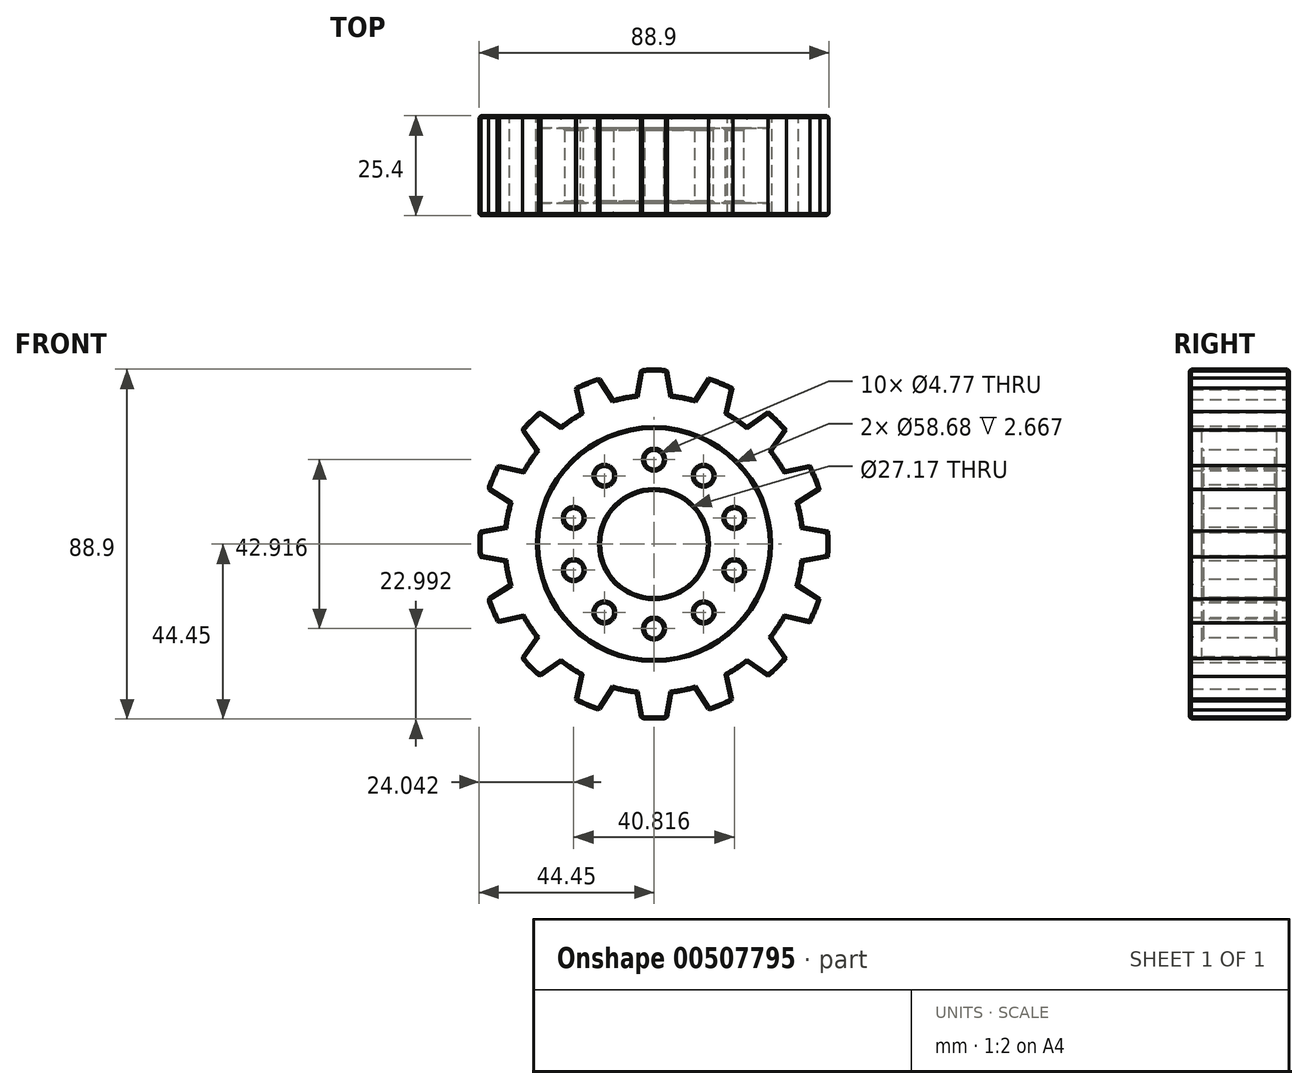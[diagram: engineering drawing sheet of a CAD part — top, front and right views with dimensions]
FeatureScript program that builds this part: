
annotation { "Feature Type Name" : "Feature", "Feature Type Description" : "" }
export const myFeature = defineFeature(function(context is Context, id is Id, definition is map)
    precondition{}
    {
        {
            var Q0;
            Q0=qCreatedBy(makeId("Front.planeOp"),FACE);
            var sketch = newSketch(context, id + "F0", { "sketchPlane" : qUnion([Q0])});
            skCircle(sketch, "E0", {"center": v(0, 0) * mm, "radius": 38.1 * mm});
            skCircle(sketch, "E1.0", {"center": v(0, 0) * mm, "radius": 44.45 * mm});
            skLineSegment(sketch, "E2", {"start": v(3.3, 44.33) * mm, "end": v(4.45, 37.84) * mm});
            skLineSegment(sketch, "E3.MirrorCS", {"start": v(-3.3, 44.33) * mm, "end": v(-4.45, 37.84) * mm});
            skLineSegment(sketch, "E4.1.0", {"start": v(-20.02, 39.69) * mm, "end": v(-18.6, 33.26) * mm});
            skLineSegment(sketch, "E4.1.1", {"start": v(-13.9, 42.22) * mm, "end": v(-10.37, 36.66) * mm});
            skLineSegment(sketch, "E4.2.0", {"start": v(-33.68, 29) * mm, "end": v(-29.9, 23.6) * mm});
            skLineSegment(sketch, "E4.2.1", {"start": v(-29, 33.68) * mm, "end": v(-23.6, 29.9) * mm});
            skLineSegment(sketch, "E4.3.0", {"start": v(-42.22, 13.9) * mm, "end": v(-36.66, 10.37) * mm});
            skLineSegment(sketch, "E4.3.1", {"start": v(-39.69, 20.02) * mm, "end": v(-33.26, 18.6) * mm});
            skLineSegment(sketch, "E4.4.0", {"start": v(-44.33, -3.3) * mm, "end": v(-37.84, -4.45) * mm});
            skLineSegment(sketch, "E4.4.1", {"start": v(-44.33, 3.3) * mm, "end": v(-37.84, 4.45) * mm});
            skLineSegment(sketch, "E4.5.0", {"start": v(-39.69, -20.02) * mm, "end": v(-33.26, -18.6) * mm});
            skLineSegment(sketch, "E4.5.1", {"start": v(-42.22, -13.9) * mm, "end": v(-36.66, -10.37) * mm});
            skLineSegment(sketch, "E4.6.0", {"start": v(-29, -33.68) * mm, "end": v(-23.6, -29.9) * mm});
            skLineSegment(sketch, "E4.6.1", {"start": v(-33.68, -29) * mm, "end": v(-29.9, -23.6) * mm});
            skLineSegment(sketch, "E4.7.0", {"start": v(-13.9, -42.22) * mm, "end": v(-10.37, -36.66) * mm});
            skLineSegment(sketch, "E4.7.1", {"start": v(-20.02, -39.69) * mm, "end": v(-18.6, -33.26) * mm});
            skLineSegment(sketch, "E4.8.0", {"start": v(3.3, -44.33) * mm, "end": v(4.45, -37.84) * mm});
            skLineSegment(sketch, "E4.8.1", {"start": v(-3.3, -44.33) * mm, "end": v(-4.45, -37.84) * mm});
            skLineSegment(sketch, "E4.9.0", {"start": v(20.02, -39.69) * mm, "end": v(18.6, -33.26) * mm});
            skLineSegment(sketch, "E4.9.1", {"start": v(13.9, -42.22) * mm, "end": v(10.37, -36.66) * mm});
            skCircle(sketch, "E5", {"center": v(0, 0) * mm, "radius": 29.34 * mm});
            skCircle(sketch, "E6", {"center": v(0, 0) * mm, "radius": 13.59 * mm});
            skCircle(sketch, "E7", {"center": v(0, 21.46) * mm, "radius": 2.39 * mm});
            skCircle(sketch, "E8.1.0", {"center": v(-12.61, 17.36) * mm, "radius": 2.39 * mm});
            skCircle(sketch, "E8.2.0", {"center": v(-20.4, 6.63) * mm, "radius": 2.39 * mm});
            skCircle(sketch, "E8.3.0", {"center": v(-20.4, -6.63) * mm, "radius": 2.39 * mm});
            skCircle(sketch, "E8.4.0", {"center": v(-12.61, -17.36) * mm, "radius": 2.39 * mm});
            skCircle(sketch, "E9.1.5.0", {"center": v(0, -21.46) * mm, "radius": 2.39 * mm});
            skCircle(sketch, "E10.1.6.0", {"center": v(12.61, -17.36) * mm, "radius": 2.39 * mm});
            skCircle(sketch, "E10.1.7.0", {"center": v(20.4, -6.63) * mm, "radius": 2.39 * mm});
            skCircle(sketch, "E11.1.8.0", {"center": v(20.4, 6.63) * mm, "radius": 2.39 * mm});
            skCircle(sketch, "E11.1.9.0", {"center": v(12.61, 17.36) * mm, "radius": 2.39 * mm});
            skLineSegment(sketch, "E12.2.10.0", {"start": v(33.68, -29) * mm, "end": v(29.9, -23.6) * mm});
            skLineSegment(sketch, "E12.3.10.0", {"start": v(29, -33.68) * mm, "end": v(23.6, -29.9) * mm});
            skLineSegment(sketch, "E12.2.11.0", {"start": v(42.22, -13.9) * mm, "end": v(36.66, -10.37) * mm});
            skLineSegment(sketch, "E12.3.11.0", {"start": v(39.69, -20.02) * mm, "end": v(33.26, -18.6) * mm});
            skLineSegment(sketch, "E13.2.12.0", {"start": v(44.33, 3.3) * mm, "end": v(37.84, 4.45) * mm});
            skLineSegment(sketch, "E13.3.12.0", {"start": v(44.33, -3.3) * mm, "end": v(37.84, -4.45) * mm});
            skLineSegment(sketch, "E14.2.13.0", {"start": v(39.69, 20.02) * mm, "end": v(33.26, 18.6) * mm});
            skLineSegment(sketch, "E14.3.13.0", {"start": v(42.22, 13.9) * mm, "end": v(36.66, 10.37) * mm});
            skLineSegment(sketch, "E15.2.14.0", {"start": v(29, 33.68) * mm, "end": v(23.6, 29.9) * mm});
            skLineSegment(sketch, "E15.3.14.0", {"start": v(33.68, 29) * mm, "end": v(29.9, 23.6) * mm});
            skLineSegment(sketch, "E16.2.15.0", {"start": v(13.9, 42.22) * mm, "end": v(10.37, 36.66) * mm});
            skLineSegment(sketch, "E16.3.15.0", {"start": v(20.02, 39.69) * mm, "end": v(18.6, 33.26) * mm});
            skSolve(sketch);
        }
        {
            var Q0;
            Q0 = qSketchRegion(id + "F0", true);
            var Q1;
            Q1=makeQuery(id+"F0.imprint","IMPRINT",FACE,{"disambiguationData":[TD([[makeQuery(id+"F0.imprint","IMPRINT",EDGE,{"derivedFrom":sQuery(id+"F0.wireOp",EDGE,"E0")}),-1.0]])]});
            extrude(context, id + "F1", {"entities" : qUnion([Q0, Q1]), "endBound" : BoundingType.SYMMETRIC, "depth" : 25.4 * mm});
        }
        {
            var Q0;
            Q0=makeQuery(id+"F0.imprint","IMPRINT",FACE,{"disambiguationData":[TD([[makeQuery(id+"F0.imprint","IMPRINT",EDGE,{"derivedFrom":sQuery(id+"F0.wireOp",EDGE,"E0")}),1.0]])]});
            extrude(context, id + "F2", {"entities" : qUnion([Q0]), "operationType" : NewBodyOperationType.ADD, "endBound" : BoundingType.SYMMETRIC, "depth" : 25.4 * mm});
        }
        {
            var Q0;
            Q0=makeQuery(id+"F0.imprint","IMPRINT",FACE,{"disambiguationData":[TD([[makeQuery(id+"F0.imprint","IMPRINT",EDGE,{"derivedFrom":sQuery(id+"F0.wireOp",EDGE,"E5")}),1.0]])]});
            extrude(context, id + "F3", {"entities" : qUnion([Q0]), "operationType" : NewBodyOperationType.ADD, "endBound" : BoundingType.SYMMETRIC, "oppositeDirection" : true, "depth" : 19.05 * mm});
        }
        {
            var Q0;
            {var subQ3=sQuery(id+"F0.wireOp",EDGE,"E4.2.1");Q0=makeQuery(id+"F0.imprint","IMPRINT",FACE,{"disambiguationData":[TD([[makeQuery(id+"F0.imprint","IMPRINT",EDGE,{"derivedFrom":subQ3}),1.0]])]});}
            var Q1;
            {var subQ3=sQuery(id+"F0.wireOp",EDGE,"E4.1.1");Q1=makeQuery(id+"F0.imprint","IMPRINT",FACE,{"disambiguationData":[TD([[makeQuery(id+"F0.imprint","IMPRINT",EDGE,{"derivedFrom":subQ3}),1.0]])]});}
            var Q2;
            {var subQ0=sQuery(id+"F0.wireOp",EDGE,"E2");Q2=makeQuery(id+"F0.imprint","IMPRINT",FACE,{"disambiguationData":[TD([[makeQuery(id+"F0.imprint","IMPRINT",EDGE,{"derivedFrom":subQ0}),1.0]])]});}
            var Q3;
            {var subQ3=sQuery(id+"F0.wireOp",EDGE,"19115ac5-5cb3-4b2e-b101-6c317fcbb66a.3.17.0");Q3=makeQuery(id+"F0.imprint","IMPRINT",FACE,{"disambiguationData":[TD([[makeQuery(id+"F0.imprint","IMPRINT",EDGE,{"derivedFrom":subQ3}),1.0]])]});}
            var Q4;
            {var subQ3=sQuery(id+"F0.wireOp",EDGE,"19115ac5-5cb3-4b2e-b101-6c317fcbb66a.3.16.0");Q4=makeQuery(id+"F0.imprint","IMPRINT",FACE,{"disambiguationData":[TD([[makeQuery(id+"F0.imprint","IMPRINT",EDGE,{"derivedFrom":subQ3}),1.0]])]});}
            var Q5;
            {var subQ3=sQuery(id+"F0.wireOp",EDGE,"19115ac5-5cb3-4b2e-b101-6c317fcbb66a.3.15.0");Q5=makeQuery(id+"F0.imprint","IMPRINT",FACE,{"disambiguationData":[TD([[makeQuery(id+"F0.imprint","IMPRINT",EDGE,{"derivedFrom":subQ3}),1.0]])]});}
            var Q6;
            {var subQ3=sQuery(id+"F0.wireOp",EDGE,"08a254bc-4d56-4bdf-b576-5eb22184e459.3.14.0");Q6=makeQuery(id+"F0.imprint","IMPRINT",FACE,{"disambiguationData":[TD([[makeQuery(id+"F0.imprint","IMPRINT",EDGE,{"derivedFrom":subQ3}),1.0]])]});}
            var Q7;
            {var subQ3=sQuery(id+"F0.wireOp",EDGE,"eef1f9f9-7af0-49e3-b1ff-47a9cc324cf0.3.13.0");Q7=makeQuery(id+"F0.imprint","IMPRINT",FACE,{"disambiguationData":[TD([[makeQuery(id+"F0.imprint","IMPRINT",EDGE,{"derivedFrom":subQ3}),1.0]])]});}
            var Q8;
            {var subQ3=sQuery(id+"F0.wireOp",EDGE,"5bd83a20-964c-4040-98d9-b5bb7ac2430a.3.12.0");Q8=makeQuery(id+"F0.imprint","IMPRINT",FACE,{"disambiguationData":[TD([[makeQuery(id+"F0.imprint","IMPRINT",EDGE,{"derivedFrom":subQ3}),1.0]])]});}
            var Q9;
            {var subQ3=sQuery(id+"F0.wireOp",EDGE,"ce90cb46-9621-431a-9bd9-97d4bde83c8d.3.11.0");Q9=makeQuery(id+"F0.imprint","IMPRINT",FACE,{"disambiguationData":[TD([[makeQuery(id+"F0.imprint","IMPRINT",EDGE,{"derivedFrom":subQ3}),1.0]])]});}
            var Q10;
            {var subQ3=sQuery(id+"F0.wireOp",EDGE,"9132d09e-f0e7-4fc6-95bd-768afe84e85a.3.10.0");Q10=makeQuery(id+"F0.imprint","IMPRINT",FACE,{"disambiguationData":[TD([[makeQuery(id+"F0.imprint","IMPRINT",EDGE,{"derivedFrom":subQ3}),1.0]])]});}
            var Q11;
            {var subQ3=sQuery(id+"F0.wireOp",EDGE,"E4.9.1");Q11=makeQuery(id+"F0.imprint","IMPRINT",FACE,{"disambiguationData":[TD([[makeQuery(id+"F0.imprint","IMPRINT",EDGE,{"derivedFrom":subQ3}),1.0]])]});}
            var Q12;
            {var subQ3=sQuery(id+"F0.wireOp",EDGE,"E4.8.1");Q12=makeQuery(id+"F0.imprint","IMPRINT",FACE,{"disambiguationData":[TD([[makeQuery(id+"F0.imprint","IMPRINT",EDGE,{"derivedFrom":subQ3}),1.0]])]});}
            var Q13;
            {var subQ3=sQuery(id+"F0.wireOp",EDGE,"E4.7.1");Q13=makeQuery(id+"F0.imprint","IMPRINT",FACE,{"disambiguationData":[TD([[makeQuery(id+"F0.imprint","IMPRINT",EDGE,{"derivedFrom":subQ3}),1.0]])]});}
            var Q14;
            {var subQ3=sQuery(id+"F0.wireOp",EDGE,"E4.6.1");Q14=makeQuery(id+"F0.imprint","IMPRINT",FACE,{"disambiguationData":[TD([[makeQuery(id+"F0.imprint","IMPRINT",EDGE,{"derivedFrom":subQ3}),1.0]])]});}
            var Q15;
            {var subQ3=sQuery(id+"F0.wireOp",EDGE,"E4.5.1");Q15=makeQuery(id+"F0.imprint","IMPRINT",FACE,{"disambiguationData":[TD([[makeQuery(id+"F0.imprint","IMPRINT",EDGE,{"derivedFrom":subQ3}),1.0]])]});}
            var Q16;
            {var subQ3=sQuery(id+"F0.wireOp",EDGE,"E4.4.1");Q16=makeQuery(id+"F0.imprint","IMPRINT",FACE,{"disambiguationData":[TD([[makeQuery(id+"F0.imprint","IMPRINT",EDGE,{"derivedFrom":subQ3}),1.0]])]});}
            var Q17;
            {var subQ3=sQuery(id+"F0.wireOp",EDGE,"E4.3.1");Q17=makeQuery(id+"F0.imprint","IMPRINT",FACE,{"disambiguationData":[TD([[makeQuery(id+"F0.imprint","IMPRINT",EDGE,{"derivedFrom":subQ3}),1.0]])]});}
            var Q18;
            {var subQ0=sQuery(id+"F0.wireOp",EDGE,"E15.2.14.0");Q18=makeQuery(id+"F0.imprint","IMPRINT",FACE,{"disambiguationData":[TD([[makeQuery(id+"F0.imprint","IMPRINT",EDGE,{"derivedFrom":subQ0}),-1.0]])]});}
            var Q19;
            {var subQ0=sQuery(id+"F0.wireOp",EDGE,"E14.2.13.0");Q19=makeQuery(id+"F0.imprint","IMPRINT",FACE,{"disambiguationData":[TD([[makeQuery(id+"F0.imprint","IMPRINT",EDGE,{"derivedFrom":subQ0}),-1.0]])]});}
            var Q20;
            {var subQ0=sQuery(id+"F0.wireOp",EDGE,"E13.2.12.0");Q20=makeQuery(id+"F0.imprint","IMPRINT",FACE,{"disambiguationData":[TD([[makeQuery(id+"F0.imprint","IMPRINT",EDGE,{"derivedFrom":subQ0}),-1.0]])]});}
            var Q21;
            {var subQ0=sQuery(id+"F0.wireOp",EDGE,"E12.2.11.0");Q21=makeQuery(id+"F0.imprint","IMPRINT",FACE,{"disambiguationData":[TD([[makeQuery(id+"F0.imprint","IMPRINT",EDGE,{"derivedFrom":subQ0}),-1.0]])]});}
            var Q22;
            {var subQ0=sQuery(id+"F0.wireOp",EDGE,"E12.2.10.0");Q22=makeQuery(id+"F0.imprint","IMPRINT",FACE,{"disambiguationData":[TD([[makeQuery(id+"F0.imprint","IMPRINT",EDGE,{"derivedFrom":subQ0}),-1.0]])]});}
            var Q23;
            {var subQ0=sQuery(id+"F0.wireOp",EDGE,"E4.9.0");Q23=makeQuery(id+"F0.imprint","IMPRINT",FACE,{"disambiguationData":[TD([[makeQuery(id+"F0.imprint","IMPRINT",EDGE,{"derivedFrom":subQ0}),-1.0]])]});}
            extrude(context, id + "F4", {"entities" : qUnion([Q0, Q1, Q2, Q3, Q4, Q5, Q6, Q7, Q8, Q9, Q10, Q11, Q12, Q13, Q14, Q15, Q16, Q17, Q18, Q19, Q20, Q21, Q22, Q23]), "operationType" : NewBodyOperationType.REMOVE, "endBound" : BoundingType.SYMMETRIC, "depth" : 25.4 * mm});
        }
        {
            var Q0;
            Q0=makeQuery(id+"F3.opExtrude","SWEPT_FACE",FACE,{"disambiguationData":[OSD([sQuery(id+"F0.wireOp",EDGE,"E8.3.0")])]});
            var Q1;
            Q1=makeQuery(id+"F3.opExtrude","SWEPT_FACE",FACE,{"disambiguationData":[OSD([sQuery(id+"F0.wireOp",EDGE,"E8.1.0")])]});
            var Q2;
            Q2=makeQuery(id+"F3.opExtrude","SWEPT_FACE",FACE,{"disambiguationData":[OSD([sQuery(id+"F0.wireOp",EDGE,"E8.2.0")])]});
            var Q3;
            {var subQ0=sQuery(id+"F0.wireOp",EDGE,"E0");Q3=makeQuery(id+"F2.boolean.opBoolean","MERGE",FACE,{"derivedFrom":[makeQuery(id+"F1.opExtrude","CAP_FACE",FACE,{"disambiguationData":[OSD([subQ0,sQuery(id+"F0.wireOp",EDGE,"E1.0")])],"isStart":false}),makeQuery(id+"F2.opExtrude","CAP_FACE",FACE,{"disambiguationData":[OSD([subQ0,sQuery(id+"F0.wireOp",EDGE,"E5")])],"isStart":false})]});}
            var Q4;
            {var subQ0=sQuery(id+"F0.wireOp",EDGE,"E0");Q4=makeQuery(id+"F2.boolean.opBoolean","MERGE",FACE,{"derivedFrom":[makeQuery(id+"F1.opExtrude","CAP_FACE",FACE,{"disambiguationData":[OSD([subQ0,sQuery(id+"F0.wireOp",EDGE,"E1.0")])],"isStart":true}),makeQuery(id+"F2.opExtrude","CAP_FACE",FACE,{"disambiguationData":[OSD([subQ0,sQuery(id+"F0.wireOp",EDGE,"E5")])],"isStart":true})]});}
            var Q5;
            {var subQ2=sQuery(id+"F0.wireOp",EDGE,"E1.0");Q5=makeQuery(id+"F4.boolean.opBoolean","SPLIT",FACE,{"disambiguationData":[TD([makeQuery(id+"F4.opExtrude","SWEPT_FACE",FACE,{"disambiguationData":[OSD([sQuery(id+"F0.wireOp",EDGE,"E4.7.0")])]})])],"derivedFrom":makeQuery(id+"F1.opExtrude","SWEPT_FACE",FACE,{"disambiguationData":[OSD([subQ2])]})});}
            var Q6;
            {var subQ2=sQuery(id+"F0.wireOp",EDGE,"E1.0");Q6=makeQuery(id+"F4.boolean.opBoolean","SPLIT",FACE,{"disambiguationData":[TD([makeQuery(id+"F4.opExtrude","SWEPT_FACE",FACE,{"disambiguationData":[OSD([sQuery(id+"F0.wireOp",EDGE,"E4.8.0")])]})])],"derivedFrom":makeQuery(id+"F1.opExtrude","SWEPT_FACE",FACE,{"disambiguationData":[OSD([subQ2])]})});}
            var Q7;
            {var subQ2=sQuery(id+"F0.wireOp",EDGE,"E1.0");Q7=makeQuery(id+"F4.boolean.opBoolean","SPLIT",FACE,{"disambiguationData":[TD([makeQuery(id+"F4.opExtrude","SWEPT_FACE",FACE,{"disambiguationData":[OSD([sQuery(id+"F0.wireOp",EDGE,"9132d09e-f0e7-4fc6-95bd-768afe84e85a.2.10.0")])]})])],"derivedFrom":makeQuery(id+"F1.opExtrude","SWEPT_FACE",FACE,{"disambiguationData":[OSD([subQ2])]})});}
            var Q8;
            {var subQ2=sQuery(id+"F0.wireOp",EDGE,"E1.0");Q8=makeQuery(id+"F4.boolean.opBoolean","SPLIT",FACE,{"disambiguationData":[TD([makeQuery(id+"F4.opExtrude","SWEPT_FACE",FACE,{"disambiguationData":[OSD([sQuery(id+"F0.wireOp",EDGE,"E4.9.0")])]})])],"derivedFrom":makeQuery(id+"F1.opExtrude","SWEPT_FACE",FACE,{"disambiguationData":[OSD([subQ2])]})});}
            var Q9;
            {var subQ2=sQuery(id+"F0.wireOp",EDGE,"E1.0");Q9=makeQuery(id+"F4.boolean.opBoolean","SPLIT",FACE,{"disambiguationData":[TD([makeQuery(id+"F4.opExtrude","SWEPT_FACE",FACE,{"disambiguationData":[OSD([sQuery(id+"F0.wireOp",EDGE,"ce90cb46-9621-431a-9bd9-97d4bde83c8d.2.11.0")])]})])],"derivedFrom":makeQuery(id+"F1.opExtrude","SWEPT_FACE",FACE,{"disambiguationData":[OSD([subQ2])]})});}
            var Q10;
            {var subQ2=sQuery(id+"F0.wireOp",EDGE,"E1.0");Q10=makeQuery(id+"F4.boolean.opBoolean","SPLIT",FACE,{"disambiguationData":[TD([makeQuery(id+"F4.opExtrude","SWEPT_FACE",FACE,{"disambiguationData":[OSD([sQuery(id+"F0.wireOp",EDGE,"5bd83a20-964c-4040-98d9-b5bb7ac2430a.2.12.0")])]})])],"derivedFrom":makeQuery(id+"F1.opExtrude","SWEPT_FACE",FACE,{"disambiguationData":[OSD([subQ2])]})});}
            var Q11;
            {var subQ2=sQuery(id+"F0.wireOp",EDGE,"E1.0");Q11=makeQuery(id+"F4.boolean.opBoolean","SPLIT",FACE,{"disambiguationData":[TD([makeQuery(id+"F4.opExtrude","SWEPT_FACE",FACE,{"disambiguationData":[OSD([sQuery(id+"F0.wireOp",EDGE,"eef1f9f9-7af0-49e3-b1ff-47a9cc324cf0.2.13.0")])]})])],"derivedFrom":makeQuery(id+"F1.opExtrude","SWEPT_FACE",FACE,{"disambiguationData":[OSD([subQ2])]})});}
            var Q12;
            {var subQ2=sQuery(id+"F0.wireOp",EDGE,"E1.0");Q12=makeQuery(id+"F4.boolean.opBoolean","SPLIT",FACE,{"disambiguationData":[TD([makeQuery(id+"F4.opExtrude","SWEPT_FACE",FACE,{"disambiguationData":[OSD([sQuery(id+"F0.wireOp",EDGE,"08a254bc-4d56-4bdf-b576-5eb22184e459.2.14.0")])]})])],"derivedFrom":makeQuery(id+"F1.opExtrude","SWEPT_FACE",FACE,{"disambiguationData":[OSD([subQ2])]})});}
            var Q13;
            {var subQ2=sQuery(id+"F0.wireOp",EDGE,"E1.0");Q13=makeQuery(id+"F4.boolean.opBoolean","SPLIT",FACE,{"disambiguationData":[TD([makeQuery(id+"F4.opExtrude","SWEPT_FACE",FACE,{"disambiguationData":[OSD([sQuery(id+"F0.wireOp",EDGE,"19115ac5-5cb3-4b2e-b101-6c317fcbb66a.2.15.0")])]})])],"derivedFrom":makeQuery(id+"F1.opExtrude","SWEPT_FACE",FACE,{"disambiguationData":[OSD([subQ2])]})});}
            var Q14;
            {var subQ2=sQuery(id+"F0.wireOp",EDGE,"E1.0");Q14=makeQuery(id+"F4.boolean.opBoolean","SPLIT",FACE,{"disambiguationData":[TD([makeQuery(id+"F4.opExtrude","SWEPT_FACE",FACE,{"disambiguationData":[OSD([sQuery(id+"F0.wireOp",EDGE,"19115ac5-5cb3-4b2e-b101-6c317fcbb66a.2.16.0")])]})])],"derivedFrom":makeQuery(id+"F1.opExtrude","SWEPT_FACE",FACE,{"disambiguationData":[OSD([subQ2])]})});}
            var Q15;
            {var subQ2=sQuery(id+"F0.wireOp",EDGE,"E1.0");Q15=makeQuery(id+"F4.boolean.opBoolean","SPLIT",FACE,{"disambiguationData":[TD([makeQuery(id+"F4.opExtrude","SWEPT_FACE",FACE,{"disambiguationData":[OSD([sQuery(id+"F0.wireOp",EDGE,"19115ac5-5cb3-4b2e-b101-6c317fcbb66a.2.17.0")])]})])],"derivedFrom":makeQuery(id+"F1.opExtrude","SWEPT_FACE",FACE,{"disambiguationData":[OSD([subQ2])]})});}
            var Q16;
            {var subQ2=sQuery(id+"F0.wireOp",EDGE,"E1.0");Q16=makeQuery(id+"F4.boolean.opBoolean","SPLIT",FACE,{"disambiguationData":[TD([makeQuery(id+"F4.opExtrude","SWEPT_FACE",FACE,{"disambiguationData":[OSD([sQuery(id+"F0.wireOp",EDGE,"E2")])]})])],"derivedFrom":makeQuery(id+"F1.opExtrude","SWEPT_FACE",FACE,{"disambiguationData":[OSD([subQ2])]})});}
            var Q17;
            {var subQ2=sQuery(id+"F0.wireOp",EDGE,"E1.0");Q17=makeQuery(id+"F4.boolean.opBoolean","SPLIT",FACE,{"disambiguationData":[TD([makeQuery(id+"F4.opExtrude","SWEPT_FACE",FACE,{"disambiguationData":[OSD([sQuery(id+"F0.wireOp",EDGE,"E4.1.0")])]})])],"derivedFrom":makeQuery(id+"F1.opExtrude","SWEPT_FACE",FACE,{"disambiguationData":[OSD([subQ2])]})});}
            var Q18;
            {var subQ2=sQuery(id+"F0.wireOp",EDGE,"E1.0");Q18=makeQuery(id+"F4.boolean.opBoolean","SPLIT",FACE,{"disambiguationData":[TD([makeQuery(id+"F4.opExtrude","SWEPT_FACE",FACE,{"disambiguationData":[OSD([sQuery(id+"F0.wireOp",EDGE,"E4.2.0")])]})])],"derivedFrom":makeQuery(id+"F1.opExtrude","SWEPT_FACE",FACE,{"disambiguationData":[OSD([subQ2])]})});}
            var Q19;
            {var subQ2=sQuery(id+"F0.wireOp",EDGE,"E1.0");Q19=makeQuery(id+"F4.boolean.opBoolean","SPLIT",FACE,{"disambiguationData":[TD([makeQuery(id+"F4.opExtrude","SWEPT_FACE",FACE,{"disambiguationData":[OSD([sQuery(id+"F0.wireOp",EDGE,"E4.3.0")])]})])],"derivedFrom":makeQuery(id+"F1.opExtrude","SWEPT_FACE",FACE,{"disambiguationData":[OSD([subQ2])]})});}
            var Q20;
            {var subQ2=sQuery(id+"F0.wireOp",EDGE,"E1.0");Q20=makeQuery(id+"F4.boolean.opBoolean","SPLIT",FACE,{"disambiguationData":[TD([makeQuery(id+"F4.opExtrude","SWEPT_FACE",FACE,{"disambiguationData":[OSD([sQuery(id+"F0.wireOp",EDGE,"E4.4.0")])]})])],"derivedFrom":makeQuery(id+"F1.opExtrude","SWEPT_FACE",FACE,{"disambiguationData":[OSD([subQ2])]})});}
            var Q21;
            {var subQ2=sQuery(id+"F0.wireOp",EDGE,"E1.0");Q21=makeQuery(id+"F4.boolean.opBoolean","SPLIT",FACE,{"disambiguationData":[TD([makeQuery(id+"F4.opExtrude","SWEPT_FACE",FACE,{"disambiguationData":[OSD([sQuery(id+"F0.wireOp",EDGE,"E4.5.0")])]})])],"derivedFrom":makeQuery(id+"F1.opExtrude","SWEPT_FACE",FACE,{"disambiguationData":[OSD([subQ2])]})});}
            var Q22;
            {var subQ2=sQuery(id+"F0.wireOp",EDGE,"E1.0");Q22=makeQuery(id+"F4.boolean.opBoolean","SPLIT",FACE,{"disambiguationData":[TD([makeQuery(id+"F4.opExtrude","SWEPT_FACE",FACE,{"disambiguationData":[OSD([sQuery(id+"F0.wireOp",EDGE,"E4.6.0")])]})])],"derivedFrom":makeQuery(id+"F1.opExtrude","SWEPT_FACE",FACE,{"disambiguationData":[OSD([subQ2])]})});}
            var Q23;
            Q23=makeQuery(id+"F3.opExtrude","SWEPT_FACE",FACE,{"disambiguationData":[OSD([sQuery(id+"F0.wireOp",EDGE,"E6")])]});
            var Q24;
            Q24=makeQuery(id+"F3.opExtrude","SWEPT_FACE",FACE,{"disambiguationData":[OSD([sQuery(id+"F0.wireOp",EDGE,"E9.1.9.0")])]});
            var Q25;
            Q25=makeQuery(id+"F3.opExtrude","SWEPT_FACE",FACE,{"disambiguationData":[OSD([sQuery(id+"F0.wireOp",EDGE,"E9.1.8.0")])]});
            var Q26;
            Q26=makeQuery(id+"F3.opExtrude","SWEPT_FACE",FACE,{"disambiguationData":[OSD([sQuery(id+"F0.wireOp",EDGE,"E9.1.7.0")])]});
            var Q27;
            Q27=makeQuery(id+"F3.opExtrude","SWEPT_FACE",FACE,{"disambiguationData":[OSD([sQuery(id+"F0.wireOp",EDGE,"E9.1.6.0")])]});
            var Q28;
            Q28=makeQuery(id+"F3.opExtrude","SWEPT_FACE",FACE,{"disambiguationData":[OSD([sQuery(id+"F0.wireOp",EDGE,"E9.1.5.0")])]});
            var Q29;
            Q29=makeQuery(id+"F3.opExtrude","SWEPT_FACE",FACE,{"disambiguationData":[OSD([sQuery(id+"F0.wireOp",EDGE,"E8.4.0")])]});
            var Q30;
            Q30=makeQuery(id+"F3.opExtrude","SWEPT_FACE",FACE,{"disambiguationData":[OSD([sQuery(id+"F0.wireOp",EDGE,"E7")])]});
            var Q31;
            Q31=makeQuery(id+"F3.opExtrude","SWEPT_FACE",FACE,{"disambiguationData":[OSD([sQuery(id+"F0.wireOp",EDGE,"E11.1.9.0")])]});
            var Q32;
            Q32=makeQuery(id+"F3.opExtrude","SWEPT_FACE",FACE,{"disambiguationData":[OSD([sQuery(id+"F0.wireOp",EDGE,"E11.1.8.0")])]});
            var Q33;
            Q33=makeQuery(id+"F3.opExtrude","SWEPT_FACE",FACE,{"disambiguationData":[OSD([sQuery(id+"F0.wireOp",EDGE,"E10.1.7.0")])]});
            var Q34;
            Q34=makeQuery(id+"F3.opExtrude","SWEPT_FACE",FACE,{"disambiguationData":[OSD([sQuery(id+"F0.wireOp",EDGE,"E10.1.6.0")])]});
            chamfer(context, id + "F5", {"entities" : qUnion([Q0, Q1, Q2, Q3, Q4, Q5, Q6, Q7, Q8, Q9, Q10, Q11, Q12, Q13, Q14, Q15, Q16, Q17, Q18, Q19, Q20, Q21, Q22, Q23, Q24, Q25, Q26, Q27, Q28, Q29, Q30, Q31, Q32, Q33, Q34]), "width" : 0.5 * mm, "tangentPropagation" : true});
        }
        {
            var Q0;
            Q0=makeQuery(id+"F4.boolean.opBoolean","COPY",EDGE,{"derivedFrom":makeQuery(id+"F4.opExtrude","SWEPT_EDGE",EDGE,{"disambiguationData":[OSD([sQuery(id+"F0.wireOp",EDGE,"E0"),sQuery(id+"F0.wireOp",EDGE,"E4.8.1")])]})});
            var Q1;
            Q1=makeQuery(id+"F4.boolean.opBoolean","COPY",EDGE,{"derivedFrom":makeQuery(id+"F4.opExtrude","SWEPT_EDGE",EDGE,{"disambiguationData":[OSD([sQuery(id+"F0.wireOp",EDGE,"E0"),sQuery(id+"F0.wireOp",EDGE,"E4.7.0")])]})});
            var Q2;
            Q2=makeQuery(id+"F4.boolean.opBoolean","COPY",EDGE,{"derivedFrom":makeQuery(id+"F4.opExtrude","SWEPT_EDGE",EDGE,{"disambiguationData":[OSD([sQuery(id+"F0.wireOp",EDGE,"E0"),sQuery(id+"F0.wireOp",EDGE,"E4.7.1")])]})});
            var Q3;
            Q3=makeQuery(id+"F4.boolean.opBoolean","COPY",EDGE,{"derivedFrom":makeQuery(id+"F4.opExtrude","SWEPT_EDGE",EDGE,{"disambiguationData":[OSD([sQuery(id+"F0.wireOp",EDGE,"E0"),sQuery(id+"F0.wireOp",EDGE,"E4.6.0")])]})});
            var Q4;
            Q4=makeQuery(id+"F4.boolean.opBoolean","COPY",EDGE,{"derivedFrom":makeQuery(id+"F4.opExtrude","SWEPT_EDGE",EDGE,{"disambiguationData":[OSD([sQuery(id+"F0.wireOp",EDGE,"E0"),sQuery(id+"F0.wireOp",EDGE,"E4.6.1")])]})});
            var Q5;
            Q5=makeQuery(id+"F4.boolean.opBoolean","COPY",EDGE,{"derivedFrom":makeQuery(id+"F4.opExtrude","SWEPT_EDGE",EDGE,{"disambiguationData":[OSD([sQuery(id+"F0.wireOp",EDGE,"E0"),sQuery(id+"F0.wireOp",EDGE,"E4.5.0")])]})});
            var Q6;
            Q6=makeQuery(id+"F4.boolean.opBoolean","COPY",EDGE,{"derivedFrom":makeQuery(id+"F4.opExtrude","SWEPT_EDGE",EDGE,{"disambiguationData":[OSD([sQuery(id+"F0.wireOp",EDGE,"E0"),sQuery(id+"F0.wireOp",EDGE,"E4.5.1")])]})});
            var Q7;
            Q7=makeQuery(id+"F4.boolean.opBoolean","COPY",EDGE,{"derivedFrom":makeQuery(id+"F4.opExtrude","SWEPT_EDGE",EDGE,{"disambiguationData":[OSD([sQuery(id+"F0.wireOp",EDGE,"E0"),sQuery(id+"F0.wireOp",EDGE,"E4.4.0")])]})});
            var Q8;
            Q8=makeQuery(id+"F4.boolean.opBoolean","COPY",EDGE,{"derivedFrom":makeQuery(id+"F4.opExtrude","SWEPT_EDGE",EDGE,{"disambiguationData":[OSD([sQuery(id+"F0.wireOp",EDGE,"E0"),sQuery(id+"F0.wireOp",EDGE,"E4.4.1")])]})});
            var Q9;
            Q9=makeQuery(id+"F4.boolean.opBoolean","COPY",EDGE,{"derivedFrom":makeQuery(id+"F4.opExtrude","SWEPT_EDGE",EDGE,{"disambiguationData":[OSD([sQuery(id+"F0.wireOp",EDGE,"E0"),sQuery(id+"F0.wireOp",EDGE,"E4.3.0")])]})});
            var Q10;
            Q10=makeQuery(id+"F4.boolean.opBoolean","COPY",EDGE,{"derivedFrom":makeQuery(id+"F4.opExtrude","SWEPT_EDGE",EDGE,{"disambiguationData":[OSD([sQuery(id+"F0.wireOp",EDGE,"E0"),sQuery(id+"F0.wireOp",EDGE,"E4.3.1")])]})});
            var Q11;
            Q11=makeQuery(id+"F4.boolean.opBoolean","COPY",EDGE,{"derivedFrom":makeQuery(id+"F4.opExtrude","SWEPT_EDGE",EDGE,{"disambiguationData":[OSD([sQuery(id+"F0.wireOp",EDGE,"E0"),sQuery(id+"F0.wireOp",EDGE,"E4.2.0")])]})});
            var Q12;
            Q12=makeQuery(id+"F4.boolean.opBoolean","COPY",EDGE,{"derivedFrom":makeQuery(id+"F4.opExtrude","SWEPT_EDGE",EDGE,{"disambiguationData":[OSD([sQuery(id+"F0.wireOp",EDGE,"E0"),sQuery(id+"F0.wireOp",EDGE,"E4.2.1")])]})});
            var Q13;
            Q13=makeQuery(id+"F4.boolean.opBoolean","COPY",EDGE,{"derivedFrom":makeQuery(id+"F4.opExtrude","SWEPT_EDGE",EDGE,{"disambiguationData":[OSD([sQuery(id+"F0.wireOp",EDGE,"E0"),sQuery(id+"F0.wireOp",EDGE,"E4.1.0")])]})});
            var Q14;
            Q14=makeQuery(id+"F4.boolean.opBoolean","COPY",EDGE,{"derivedFrom":makeQuery(id+"F4.opExtrude","SWEPT_EDGE",EDGE,{"disambiguationData":[OSD([sQuery(id+"F0.wireOp",EDGE,"E0"),sQuery(id+"F0.wireOp",EDGE,"E4.1.1")])]})});
            var Q15;
            Q15=makeQuery(id+"F4.boolean.opBoolean","COPY",EDGE,{"derivedFrom":makeQuery(id+"F4.opExtrude","SWEPT_EDGE",EDGE,{"disambiguationData":[OSD([sQuery(id+"F0.wireOp",EDGE,"E0"),sQuery(id+"F0.wireOp",EDGE,"E3.MirrorCS")])]})});
            var Q16;
            Q16=makeQuery(id+"F4.boolean.opBoolean","COPY",EDGE,{"derivedFrom":makeQuery(id+"F4.opExtrude","SWEPT_EDGE",EDGE,{"disambiguationData":[OSD([sQuery(id+"F0.wireOp",EDGE,"E0"),sQuery(id+"F0.wireOp",EDGE,"E2")])]})});
            var Q17;
            Q17=makeQuery(id+"F4.boolean.opBoolean","COPY",EDGE,{"derivedFrom":makeQuery(id+"F4.opExtrude","SWEPT_EDGE",EDGE,{"disambiguationData":[OSD([sQuery(id+"F0.wireOp",EDGE,"E0"),sQuery(id+"F0.wireOp",EDGE,"19115ac5-5cb3-4b2e-b101-6c317fcbb66a.2.17.0")])]})});
            var Q18;
            Q18=makeQuery(id+"F4.boolean.opBoolean","COPY",EDGE,{"derivedFrom":makeQuery(id+"F4.opExtrude","SWEPT_EDGE",EDGE,{"disambiguationData":[OSD([sQuery(id+"F0.wireOp",EDGE,"E0"),sQuery(id+"F0.wireOp",EDGE,"19115ac5-5cb3-4b2e-b101-6c317fcbb66a.3.17.0")])]})});
            var Q19;
            Q19=makeQuery(id+"F4.boolean.opBoolean","COPY",EDGE,{"derivedFrom":makeQuery(id+"F4.opExtrude","SWEPT_EDGE",EDGE,{"disambiguationData":[OSD([sQuery(id+"F0.wireOp",EDGE,"E0"),sQuery(id+"F0.wireOp",EDGE,"19115ac5-5cb3-4b2e-b101-6c317fcbb66a.2.16.0")])]})});
            var Q20;
            Q20=makeQuery(id+"F4.boolean.opBoolean","COPY",EDGE,{"derivedFrom":makeQuery(id+"F4.opExtrude","SWEPT_EDGE",EDGE,{"disambiguationData":[OSD([sQuery(id+"F0.wireOp",EDGE,"E0"),sQuery(id+"F0.wireOp",EDGE,"19115ac5-5cb3-4b2e-b101-6c317fcbb66a.3.16.0")])]})});
            var Q21;
            Q21=makeQuery(id+"F4.boolean.opBoolean","COPY",EDGE,{"derivedFrom":makeQuery(id+"F4.opExtrude","SWEPT_EDGE",EDGE,{"disambiguationData":[OSD([sQuery(id+"F0.wireOp",EDGE,"E0"),sQuery(id+"F0.wireOp",EDGE,"19115ac5-5cb3-4b2e-b101-6c317fcbb66a.2.15.0")])]})});
            var Q22;
            Q22=makeQuery(id+"F4.boolean.opBoolean","COPY",EDGE,{"derivedFrom":makeQuery(id+"F4.opExtrude","SWEPT_EDGE",EDGE,{"disambiguationData":[OSD([sQuery(id+"F0.wireOp",EDGE,"E0"),sQuery(id+"F0.wireOp",EDGE,"19115ac5-5cb3-4b2e-b101-6c317fcbb66a.3.15.0")])]})});
            var Q23;
            Q23=makeQuery(id+"F4.boolean.opBoolean","COPY",EDGE,{"derivedFrom":makeQuery(id+"F4.opExtrude","SWEPT_EDGE",EDGE,{"disambiguationData":[OSD([sQuery(id+"F0.wireOp",EDGE,"E0"),sQuery(id+"F0.wireOp",EDGE,"08a254bc-4d56-4bdf-b576-5eb22184e459.2.14.0")])]})});
            var Q24;
            Q24=makeQuery(id+"F4.boolean.opBoolean","COPY",EDGE,{"derivedFrom":makeQuery(id+"F4.opExtrude","SWEPT_EDGE",EDGE,{"disambiguationData":[OSD([sQuery(id+"F0.wireOp",EDGE,"E0"),sQuery(id+"F0.wireOp",EDGE,"08a254bc-4d56-4bdf-b576-5eb22184e459.3.14.0")])]})});
            var Q25;
            Q25=makeQuery(id+"F4.boolean.opBoolean","COPY",EDGE,{"derivedFrom":makeQuery(id+"F4.opExtrude","SWEPT_EDGE",EDGE,{"disambiguationData":[OSD([sQuery(id+"F0.wireOp",EDGE,"E0"),sQuery(id+"F0.wireOp",EDGE,"eef1f9f9-7af0-49e3-b1ff-47a9cc324cf0.2.13.0")])]})});
            var Q26;
            Q26=makeQuery(id+"F4.boolean.opBoolean","COPY",EDGE,{"derivedFrom":makeQuery(id+"F4.opExtrude","SWEPT_EDGE",EDGE,{"disambiguationData":[OSD([sQuery(id+"F0.wireOp",EDGE,"E0"),sQuery(id+"F0.wireOp",EDGE,"eef1f9f9-7af0-49e3-b1ff-47a9cc324cf0.3.13.0")])]})});
            var Q27;
            Q27=makeQuery(id+"F4.boolean.opBoolean","COPY",EDGE,{"derivedFrom":makeQuery(id+"F4.opExtrude","SWEPT_EDGE",EDGE,{"disambiguationData":[OSD([sQuery(id+"F0.wireOp",EDGE,"E0"),sQuery(id+"F0.wireOp",EDGE,"5bd83a20-964c-4040-98d9-b5bb7ac2430a.2.12.0")])]})});
            var Q28;
            Q28=makeQuery(id+"F4.boolean.opBoolean","COPY",EDGE,{"derivedFrom":makeQuery(id+"F4.opExtrude","SWEPT_EDGE",EDGE,{"disambiguationData":[OSD([sQuery(id+"F0.wireOp",EDGE,"E0"),sQuery(id+"F0.wireOp",EDGE,"5bd83a20-964c-4040-98d9-b5bb7ac2430a.3.12.0")])]})});
            var Q29;
            Q29=makeQuery(id+"F4.boolean.opBoolean","COPY",EDGE,{"derivedFrom":makeQuery(id+"F4.opExtrude","SWEPT_EDGE",EDGE,{"disambiguationData":[OSD([sQuery(id+"F0.wireOp",EDGE,"E0"),sQuery(id+"F0.wireOp",EDGE,"ce90cb46-9621-431a-9bd9-97d4bde83c8d.2.11.0")])]})});
            var Q30;
            Q30=makeQuery(id+"F4.boolean.opBoolean","COPY",EDGE,{"derivedFrom":makeQuery(id+"F4.opExtrude","SWEPT_EDGE",EDGE,{"disambiguationData":[OSD([sQuery(id+"F0.wireOp",EDGE,"E0"),sQuery(id+"F0.wireOp",EDGE,"ce90cb46-9621-431a-9bd9-97d4bde83c8d.3.11.0")])]})});
            var Q31;
            Q31=makeQuery(id+"F4.boolean.opBoolean","COPY",EDGE,{"derivedFrom":makeQuery(id+"F4.opExtrude","SWEPT_EDGE",EDGE,{"disambiguationData":[OSD([sQuery(id+"F0.wireOp",EDGE,"E0"),sQuery(id+"F0.wireOp",EDGE,"9132d09e-f0e7-4fc6-95bd-768afe84e85a.2.10.0")])]})});
            var Q32;
            Q32=makeQuery(id+"F4.boolean.opBoolean","COPY",EDGE,{"derivedFrom":makeQuery(id+"F4.opExtrude","SWEPT_EDGE",EDGE,{"disambiguationData":[OSD([sQuery(id+"F0.wireOp",EDGE,"E0"),sQuery(id+"F0.wireOp",EDGE,"9132d09e-f0e7-4fc6-95bd-768afe84e85a.3.10.0")])]})});
            var Q33;
            Q33=makeQuery(id+"F4.boolean.opBoolean","COPY",EDGE,{"derivedFrom":makeQuery(id+"F4.opExtrude","SWEPT_EDGE",EDGE,{"disambiguationData":[OSD([sQuery(id+"F0.wireOp",EDGE,"E0"),sQuery(id+"F0.wireOp",EDGE,"E4.9.0")])]})});
            var Q34;
            Q34=makeQuery(id+"F4.boolean.opBoolean","COPY",EDGE,{"derivedFrom":makeQuery(id+"F4.opExtrude","SWEPT_EDGE",EDGE,{"disambiguationData":[OSD([sQuery(id+"F0.wireOp",EDGE,"E0"),sQuery(id+"F0.wireOp",EDGE,"E4.9.1")])]})});
            var Q35;
            Q35=makeQuery(id+"F4.boolean.opBoolean","COPY",EDGE,{"derivedFrom":makeQuery(id+"F4.opExtrude","SWEPT_EDGE",EDGE,{"disambiguationData":[OSD([sQuery(id+"F0.wireOp",EDGE,"E0"),sQuery(id+"F0.wireOp",EDGE,"E4.8.0")])]})});
            fillet(context, id + "F6", {"entities" : qUnion([Q0, Q1, Q2, Q3, Q4, Q5, Q6, Q7, Q8, Q9, Q10, Q11, Q12, Q13, Q14, Q15, Q16, Q17, Q18, Q19, Q20, Q21, Q22, Q23, Q24, Q25, Q26, Q27, Q28, Q29, Q30, Q31, Q32, Q33, Q34, Q35]), "radius" : 0.5 * mm, "tangentPropagation" : true, "allowEdgeOverflow" : false});
        }
    });
